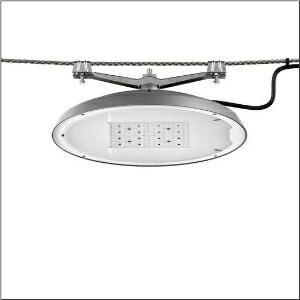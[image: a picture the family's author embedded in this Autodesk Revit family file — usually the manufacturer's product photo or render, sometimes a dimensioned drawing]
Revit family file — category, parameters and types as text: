
# Revit family: dl_50_iq_mini___st0_8s_5xa248v41f08le_2aff
name_source: partatom
category: Lighting Fixtures
units: mm (PartAtom-declared; Revit-internal decimal feet)

## family parameters
Cut with Voids When Loaded = No
Host = Face
Light Source = No
Part Type = Normal
Room Calculation Point = No
Round Connector Dimension = Use Diameter
Shared = No

## types (1)
- --- (1 x LED, 10390 lm, 64.1 W, 4000K)
    Apparent Load = 64 VA
    CIE Flux Codes = 38 75 97 100 100
    Color Rendering = 70
    Color Temperature = 4000K
    Default Elevation = 1800 mm
    Description = DL 50 iQ mini, catenary luminaire, primary light control with lens, of PMMA, primary optical cover: cover, of toughened safety glass, transparent, light distribution: ST0.8s, light emission: direct distribution, primary light characteristic: symmetric, installation type: suspended mounting, LED, High Power LED, rated luminous flux: 10.390lm, luminous efficacy: 162lm/W, light colour: 740, colour temperature: 4000K, control gear: iQ Street-Remote, control: optimised constant luminous flux control (CLO 2.0), Desk-Remote (wireless, voltage-free reading and setting of iQ features in the workshop via application-optimized NFC function/RFID function), Light-Fading, Smart-Wire, Night-Set, Lumen-Switch, Temp-Guard, Auto-Match, Street-Remote, mains connection: 230..240V, AC, 50/60Hz, start of lifetime: 64W, end of service life: 67W, reduction: 30W, luminaire housing, of diecast aluminium, powder-coated, SITECO metallic grey (DB 702S), diameter: 500mm, height: 115mm, mounting height: 4..12m, protection rating (complete): IP66, insulation class (complete): insulation class II (safety insulation), certification: CE, ENEC, ENEC+, VDE, impact resistance: IK08, permissible operating ambient temperature for outdoor applications: -25..+40°C, standard-compliant lighting for roads and squares, packaging unit: 1 piece

Light Distribution: ST0.8s
    Height = 124 mm  [stored 0.406824 ft]
    Lamp = 1 x LED
    Lamp Light Flux = 10390 lm
    Lamp Power = 64.1 W
    Lamp count = 1
    Length = 500 mm
    Luminous efficacy = 162 lm/W
    Manufacturer = Siteco
    ModVariant = No
    Model = 5XA248V41F08LE
    Number of Poles = 1
    OnlyDefault = Yes
    Power Factor = 1
    Product Name = DL 50 iQ mini | ST0.8s
    Product group = catenary luminaire
    ProductGroupID = 6300
    Protection Class = Protection class II
    Protection Degree = IP 66
    RLX_Detail_Level = 1
    RLX_Emergency_Light_Flux = 0 lm
    RLX_Emergency_Type = 0
    RLX_Emergency_Type_DB = No
    RlxData = <blob elided: 127097 chars, md5=9481e4b8>
    Socket = socket
    Standby Power = 0 W
    System Light Flux = 10390 lm
    System Power = 64 W
    Type Comments = factory setting: luminous flux: 100 % | dim-lin: 254 | 672 mA
    Type Image = l_1251783.jpg
    URL = http://relux.com
    VarID = @adj_140515
    Voltage = 0 V
    Weight = 0.00 kg
    Width = 0 mm  [stored 0 ft]

note: [stored X ft] marks values corroborated as IEEE doubles in the binary element streams (Revit-internal decimal feet)

## geometry (parser evidence)
native form markers: Blend x4, Sweep x14
no freeform markers — native parametric forms only
